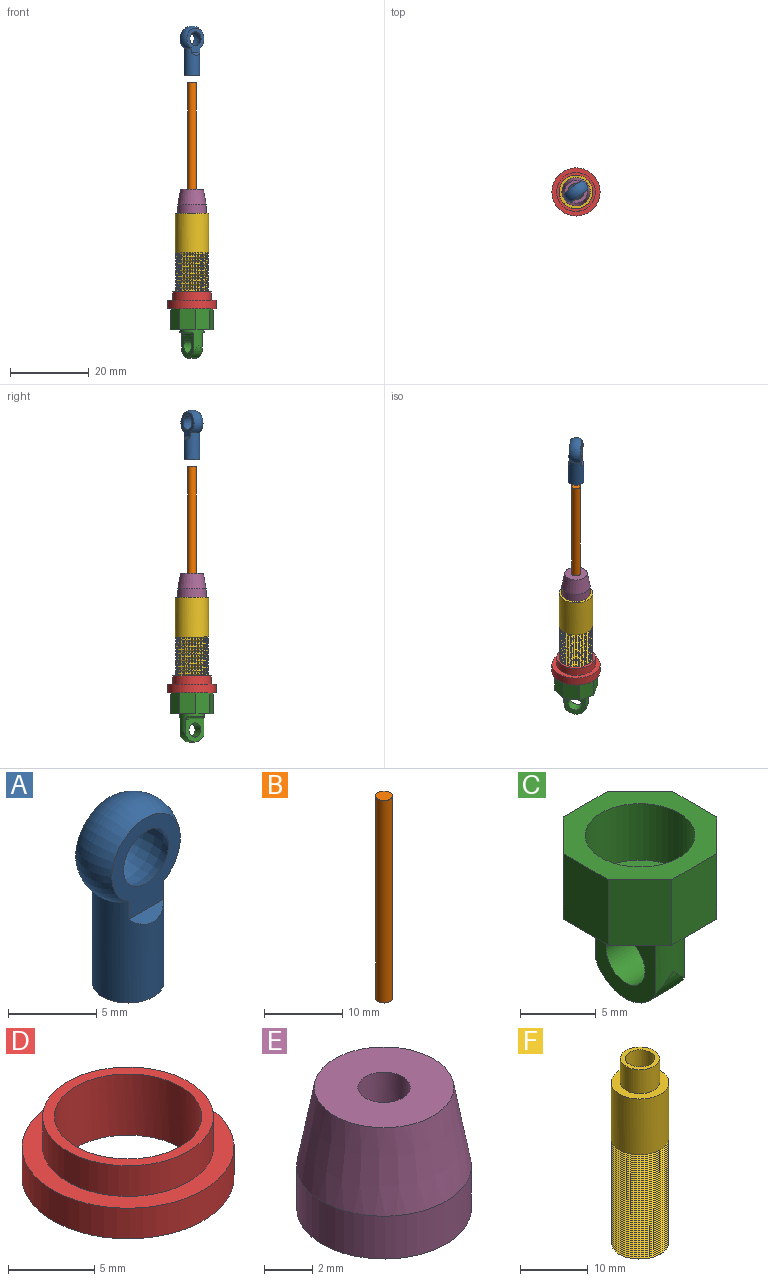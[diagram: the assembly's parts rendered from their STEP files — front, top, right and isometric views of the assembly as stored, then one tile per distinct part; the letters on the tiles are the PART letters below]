
ASSEMBLY  parts=6 mates=9
PART A: 10 faces, bbox 6.5x4x12.1 mm
  f0: cylinder r=2.02mm len=7.04mm, axis (0,0,1), area 78.3mm2, adj f1,f2,f3,f5,f8,f9
  f1: plane 6.35x5.48mm, normal (0,-1,0), area 16.2mm2, adj f0,f2,f4,f8
  f2: torus R=0.95mm, axis (0,1,0), area 48.2mm2, adj f0,f1,f3
  f3: plane 6.35x5.48mm, normal (0,1,0), area 16.2mm2, adj f0,f2,f4,f9
  f4: revolved ~4.33x4.33mm, area 38.6mm2, adj f1,f3
  f5: plane 4.04x4.04mm, normal (0,0,-1), area 9.2mm2, adj f0,f7
  f6: torus R=0.95mm, axis (0,1,0), area 3.9mm2, adj f7
  f7: cylinder r=1.08mm len=6.41mm, axis (0,0,-1), area 43.3mm2, adj f5,f6
  f8: plane 2.83x0.58mm, normal (0,-0.71,0.71), area 1.6mm2, adj f0,f1
  f9: plane 2.83x0.58mm, normal (0,0.71,0.71), area 1.6mm2, adj f0,f3
PART B: 3 faces, bbox 2.2x2.2x31.7 mm
  f0: cylinder r=1.08mm len=31.71mm, axis (0,0,-1), area 215.8mm2, adj f1,f2
  f1: plane 2.17x2.17mm, normal (0,0,-1), area 3.7mm2, adj f0
  f2: plane 2.17x2.17mm, normal (0,0,1), area 3.7mm2, adj f0
PART C: 21 faces, bbox 10.1x10.1x12.5 mm
  f0: cylinder r=3.07mm len=6.14mm, axis (0,0,1), area 37.1mm2, adj f1,f2,f12,f15,f16,f18,f19,f20
  f1: plane 5.78x5.53mm, normal (1,0,0), area 19mm2, adj f0,f17,f18,f19
  f2: plane 5.78x5.53mm, normal (-1,0,0), area 19mm2, adj f0,f17,f18,f20
  f3: plane 5.27x4.19mm, normal (0,-1,0), area 22.1mm2, adj f4,f10,f11,f12
  f4: plane 5.27x2.96mm, normal (0.71,-0.71,0), area 22.1mm2, adj f3,f5,f11,f12
  f5: plane 5.27x4.19mm, normal (1,0,0), area 22.1mm2, adj f4,f6,f11,f12
  f6: plane 5.27x2.96mm, normal (0.71,0.71,0), area 22.1mm2, adj f5,f7,f11,f12
  f7: plane 5.27x4.19mm, normal (0,1,0), area 22.1mm2, adj f6,f8,f11,f12
  f8: plane 5.27x2.96mm, normal (-0.71,0.71,0), area 22.1mm2, adj f7,f9,f11,f12
  f9: plane 5.27x4.19mm, normal (-1,0,0), area 22.1mm2, adj f8,f10,f11,f12
  f10: plane 5.27x2.96mm, normal (-0.71,-0.71,0), area 22.1mm2, adj f3,f9,f11,f12
  f11: plane 10.11x10.11mm, normal (0,0,1), area 43.7mm2, adj f3,f4,f5,f6,f7,f8,f9,f10
  f12: plane 10.11x10.11mm, normal (0,0,-1), area 55.1mm2, adj f0,f3,f4,f5,f6,f7,f8,f9
  f13: cylinder r=3.61mm len=7.22mm, axis (0,0,1), area 103.2mm2, adj f11,f14
  f14: plane 7.22x7.22mm, normal (0,0,1), area 40.9mm2, adj f13
  f15: plane 4.55x1.01mm, normal (0,0,-1), area 3.2mm2, adj f0,f19
  f16: plane 4.55x1.01mm, normal (0,0,-1), area 3.2mm2, adj f0,f20
  f17: cylinder r=1.8mm len=3.61mm, axis (-1,0,0), area 30.3mm2, adj f1,f2
  f18: cylinder r=3.07mm len=6.14mm, axis (-1,0,0), area 22.1mm2, adj f0,f1,f2
  f19: cylinder r=0.72mm len=5.53mm, axis (0,1,0), area 5.9mm2, adj f0,f1,f15
  f20: cylinder r=0.72mm len=5.53mm, axis (0,-1,0), area 5.9mm2, adj f0,f2,f16
PART D: 6 faces, bbox 12.3x12.3x4.3 mm
  f0: cylinder r=6.14mm len=12.27mm, axis (0,0,-1), area 83.5mm2, adj f1,f2
  f1: plane 12.27x12.27mm, normal (0,0,1), area 41.5mm2, adj f0,f3
  f2: plane 12.27x12.27mm, normal (0,0,-1), area 61.3mm2, adj f0,f5
  f3: cylinder r=4.95mm len=9.89mm, axis (0,0,-1), area 67.3mm2, adj f1,f4
  f4: plane 9.89x9.89mm, normal (0,0,1), area 19.8mm2, adj f3,f5
  f5: cylinder r=4.26mm len=8.52mm, axis (0,0,-1), area 115.9mm2, adj f2,f4
PART E: 7 faces, bbox 7.2x7.2x6.1 mm
  f0: cylinder r=3.61mm len=7.22mm, axis (0,0,-1), area 49.1mm2, adj f1,f3
  f1: plane 7.22x7.22mm, normal (0,0,-1), area 14.7mm2, adj f0,f4
  f2: plane 5.78x5.78mm, normal (0,0,1), area 22.5mm2, adj f3,f6
  f3: cone r=3.61mm half-angle=10.3deg, axis (0,0,-1), area 82.4mm2, adj f0,f2
  f4: cylinder r=2.89mm len=5.78mm, axis (0,0,-1), area 78.6mm2, adj f1,f5
  f5: plane 5.78x5.78mm, normal (0,0,-1), area 22.5mm2, adj f4,f6
  f6: cylinder r=1.08mm len=2.17mm, axis (0,0,-1), area 12.3mm2, adj f2,f5
PART F: 66 faces, bbox 8.8x10.2x33.7 mm
  f0: cylinder r=4.26mm len=10.29mm, axis (0,0,-1), area 270.7mm2, adj f52,f53,f63,f64
  f1: cylinder r=4.26mm len=8.52mm, axis (0,0,-1), area 0.1mm2, adj f2,f54,f62,f65
  f2: cylinder r=4.26mm len=8.52mm, axis (0,0,-1), area 0.2mm2, adj f1,f3,f62,f64
  f3: cylinder r=4.26mm len=8.52mm, axis (0,0,-1), area 0.2mm2, adj f2,f4,f62,f64
  f4: cylinder r=4.26mm len=8.52mm, axis (0,0,-1), area 0.2mm2, adj f3,f5,f62,f64
  f5: cylinder r=4.26mm len=8.52mm, axis (0,0,-1), area 0.2mm2, adj f4,f6,f62,f64
  f6: cylinder r=4.26mm len=8.52mm, axis (0,0,-1), area 0.2mm2, adj f5,f7,f62,f64
  f7: cylinder r=4.26mm len=8.52mm, axis (0,0,-1), area 0.2mm2, adj f6,f8,f62,f64
  f8: cylinder r=4.26mm len=8.52mm, axis (0,0,-1), area 0.2mm2, adj f7,f9,f62,f64
  f9: cylinder r=4.26mm len=8.52mm, axis (0,0,-1), area 0.2mm2, adj f8,f10,f62,f64
  f10: cylinder r=4.26mm len=8.52mm, axis (0,0,-1), area 0.2mm2, adj f9,f11,f62,f64
  f11: cylinder r=4.26mm len=8.52mm, axis (0,0,-1), area 0.2mm2, adj f10,f12,f62,f64
  f12: cylinder r=4.26mm len=8.52mm, axis (0,0,-1), area 0.2mm2, adj f11,f13,f62,f64
  f13: cylinder r=4.26mm len=8.52mm, axis (0,0,-1), area 0.2mm2, adj f12,f14,f62,f64
  f14: cylinder r=4.26mm len=8.52mm, axis (0,0,-1), area 0.2mm2, adj f13,f15,f62,f64
  f15: cylinder r=4.26mm len=8.52mm, axis (0,0,-1), area 0.2mm2, adj f14,f16,f62,f64
  f16: cylinder r=4.26mm len=8.52mm, axis (0,0,-1), area 0.2mm2, adj f15,f17,f62,f64
  f17: cylinder r=4.26mm len=8.52mm, axis (0,0,-1), area 0.2mm2, adj f16,f18,f62,f64
  f18: cylinder r=4.26mm len=8.52mm, axis (0,0,-1), area 0.2mm2, adj f17,f19,f62,f64
  f19: cylinder r=4.26mm len=8.52mm, axis (0,0,-1), area 0.2mm2, adj f18,f20,f62,f64
  f20: cylinder r=4.26mm len=8.52mm, axis (0,0,-1), area 0.2mm2, adj f19,f21,f62,f64
  f21: cylinder r=4.26mm len=8.52mm, axis (0,0,-1), area 0.2mm2, adj f20,f22,f62,f64
  f22: cylinder r=4.26mm len=8.52mm, axis (0,0,-1), area 0.2mm2, adj f21,f23,f62,f64
  f23: cylinder r=4.26mm len=8.52mm, axis (0,0,-1), area 0.2mm2, adj f22,f24,f62,f64
  f24: cylinder r=4.26mm len=8.52mm, axis (0,0,-1), area 0.2mm2, adj f23,f25,f62,f64
  f25: cylinder r=4.26mm len=8.52mm, axis (0,0,-1), area 0.2mm2, adj f24,f26,f62,f64
  f26: cylinder r=4.26mm len=8.52mm, axis (0,0,-1), area 0.2mm2, adj f25,f27,f62,f64
  f27: cylinder r=4.26mm len=8.52mm, axis (0,0,-1), area 0.2mm2, adj f26,f28,f62,f64
  f28: cylinder r=4.26mm len=8.52mm, axis (0,0,-1), area 0.2mm2, adj f27,f29,f62,f64
  f29: cylinder r=4.26mm len=8.52mm, axis (0,0,-1), area 0.2mm2, adj f28,f30,f62,f64
  f30: cylinder r=4.26mm len=8.52mm, axis (0,0,-1), area 0.2mm2, adj f29,f31,f62,f64
  f31: cylinder r=4.26mm len=8.52mm, axis (0,0,-1), area 0.2mm2, adj f30,f32,f62,f64
  f32: cylinder r=4.26mm len=8.52mm, axis (0,0,-1), area 0.2mm2, adj f31,f33,f62,f64
  f33: cylinder r=4.26mm len=8.52mm, axis (0,0,-1), area 0.2mm2, adj f32,f34,f62,f64
  f34: cylinder r=4.26mm len=8.52mm, axis (0,0,-1), area 0.2mm2, adj f33,f35,f62,f64
  f35: cylinder r=4.26mm len=8.52mm, axis (0,0,-1), area 0.2mm2, adj f34,f36,f62,f64
  f36: cylinder r=4.26mm len=8.52mm, axis (0,0,-1), area 0.2mm2, adj f35,f37,f62,f64
  f37: cylinder r=4.26mm len=8.52mm, axis (0,0,-1), area 0.2mm2, adj f36,f38,f62,f64
  f38: cylinder r=4.26mm len=8.52mm, axis (0,0,-1), area 0.2mm2, adj f37,f39,f62,f64
  f39: cylinder r=4.26mm len=8.52mm, axis (0,0,-1), area 0.2mm2, adj f38,f40,f62,f64
  f40: cylinder r=4.26mm len=8.52mm, axis (0,0,-1), area 0.2mm2, adj f39,f41,f62,f64
  f41: cylinder r=4.26mm len=8.52mm, axis (0,0,-1), area 0.2mm2, adj f40,f42,f62,f64
  f42: cylinder r=4.26mm len=8.52mm, axis (0,0,-1), area 0.2mm2, adj f41,f43,f62,f64
  f43: cylinder r=4.26mm len=8.52mm, axis (0,0,-1), area 0.2mm2, adj f42,f44,f62,f64
  f44: cylinder r=4.26mm len=8.52mm, axis (0,0,-1), area 0.2mm2, adj f43,f45,f62,f64
  f45: cylinder r=4.26mm len=8.52mm, axis (0,0,-1), area 0.2mm2, adj f44,f46,f62,f64
  f46: cylinder r=4.26mm len=8.52mm, axis (0,0,-1), area 0.2mm2, adj f45,f47,f62,f64
  f47: cylinder r=4.26mm len=8.52mm, axis (0,0,-1), area 0.2mm2, adj f46,f48,f62,f64
  f48: cylinder r=4.26mm len=8.52mm, axis (0,0,-1), area 0.2mm2, adj f47,f49,f62,f64
  f49: cylinder r=4.26mm len=8.52mm, axis (0,0,-1), area 0.2mm2, adj f48,f50,f62,f64
  f50: cylinder r=4.26mm len=8.52mm, axis (0,0,-1), area 0.2mm2, adj f49,f51,f62,f64
  f51: cylinder r=4.26mm len=8.52mm, axis (0,0,-1), area 0.2mm2, adj f50,f52,f62,f64
  f52: cylinder r=4.26mm len=8.52mm, axis (0,0,-1), area 0.2mm2, adj f0,f51,f62,f64
  f53: plane 8.52x8.52mm, normal (0,0,1), area 30.8mm2, adj f0,f55
  f54: plane 8.5x8.48mm, normal (0,0,-1), area 11.5mm2, adj f1,f61,f62,f65
  f55: cylinder r=2.89mm len=5.78mm, axis (0,0,-1), area 78.6mm2, adj f53,f56
  f56: plane 5.78x5.78mm, normal (0,0,1), area 11.5mm2, adj f55,f57
  f57: cylinder r=2.17mm len=4.33mm, axis (0,0,1), area 49.1mm2, adj f56,f58
  f58: plane 4.33x4.33mm, normal (0,0,1), area 11.1mm2, adj f57,f59
  f59: cylinder r=1.08mm len=2.17mm, axis (0,0,1), area 9.8mm2, adj f58,f60
  f60: plane 7.22x7.22mm, normal (0,0,-1), area 37.3mm2, adj f59,f61
  f61: cylinder r=3.61mm len=28.16mm, axis (0,0,-1), area 638.7mm2, adj f54,f60
  f62: bspline ~18.95x9.84mm, area 528.3mm2, adj f1,f2,f3,f4,f5,f6,f7,f8
  f63: plane 0.36x0.35mm, normal (0,-1,0), area 0.1mm2, adj f0,f62,f64
  f64: bspline ~18.95x9.84mm, area 535.3mm2, adj f0,f2,f3,f4,f5,f6,f7,f8
  f65: bspline ~8.52x4.92mm, area 2.5mm2, adj f1,f54,f64
PLACE A rot(axis=(0,0,-1),142.5deg) t=(-8.93,-6.71,64.97)mm
PLACE B rot(axis=(0,0,-1),167.9deg) t=(-9.81,-5.56,22.01)mm
PLACE C rot(axis=(0,0,-1),146.9deg) t=(-9.81,-5.56,-9.16)mm
PLACE D rot(axis=(0,0,-1),75.6deg) t=(-9.81,-5.56,-3.89)mm
PLACE E rot(axis=(0,0,1),127.5deg) t=(-9.81,-5.56,20.45)mm
PLACE F t=(-9.81,-5.56,-8.43)mm fixed
MATE cylindrical C.f13 <-> F.f0  axis (0,0,1) through (-9.81,-5.56,-3.89)mm
MATE planar C.f13 <-> F.f54  axis (0,0,1) through (-9.81,-5.56,-8.43)mm
MATE cylindrical D.f5 <-> F.f0  axis (0,0,-1) through (-9.81,-5.56,-3.89)mm
MATE slider A.f0 <-> E.f0  axis (0,0,1) through (-9.81,-5.56,55.58)mm
MATE cylindrical A.f0 <-> F.f55  axis (0,0,1) through (-9.81,-5.56,59.12)mm
MATE cylindrical B.f0 <-> A.f0  axis (0,0,-1) through (-9.81,-5.56,37.86)mm
MATE cylindrical E.f0 <-> F.f55  axis (0,0,-1) through (-9.81,-5.56,21.53)mm
MATE planar D.f0 <-> C.f13  axis (0,0,-1) through (-9.81,-5.56,-3.89)mm
MATE planar E.f0 <-> F.f0  axis (0,0,-1) through (-9.81,-5.56,20.45)mm
